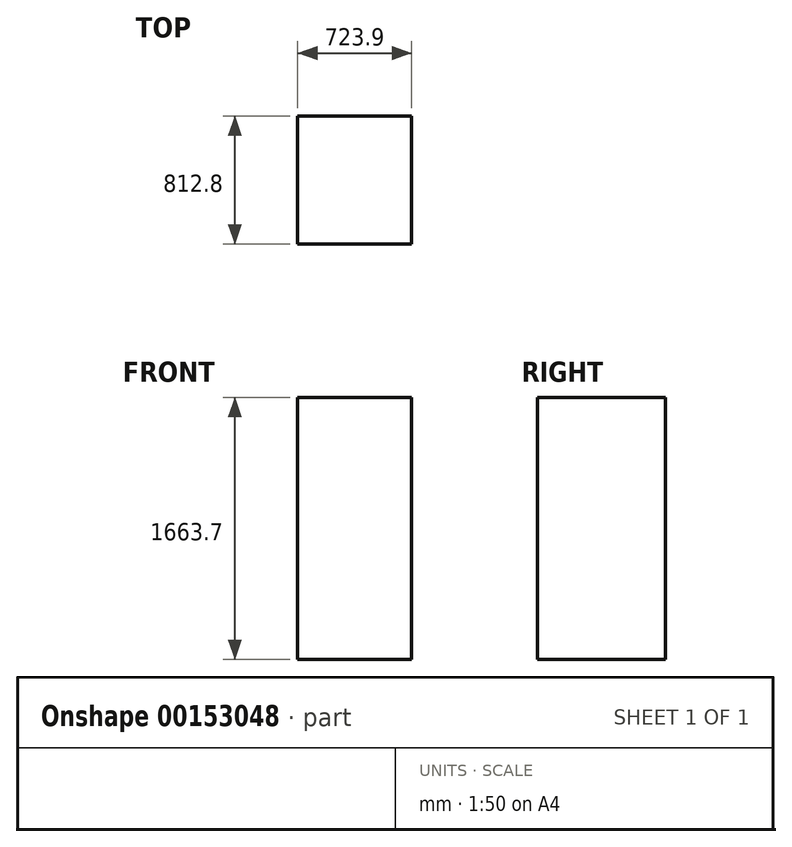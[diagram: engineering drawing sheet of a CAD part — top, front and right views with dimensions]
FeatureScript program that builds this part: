
annotation { "Feature Type Name" : "Feature", "Feature Type Description" : "" }
export const myFeature = defineFeature(function(context is Context, id is Id, definition is map)
    precondition{}
    {
        {
            var Q0;
            Q0=qCreatedBy(makeId("Top.planeOp"),FACE);
            var sketch = newSketch(context, id + "F0", { "sketchPlane" : qUnion([Q0])});
            skLineSegment(sketch, "E0.bottom", {"start": v(0, 0) * mm, "end": v(-723.9, 0) * mm});
            skLineSegment(sketch, "E0.top", {"start": v(0, -812.8) * mm, "end": v(-723.9, -812.8) * mm});
            skLineSegment(sketch, "E0.left", {"start": v(0, 0) * mm, "end": v(0, -812.8) * mm});
            skLineSegment(sketch, "E0.right", {"start": v(-723.9, 0) * mm, "end": v(-723.9, -812.8) * mm});
            skSolve(sketch);
        }
        {
            var Q0;
            Q0 = qSketchRegion(id + "F0", true);
            extrude(context, id + "F1", {"entities" : qUnion([Q0]), "depth" : 1663.7 * mm});
        }
    });
